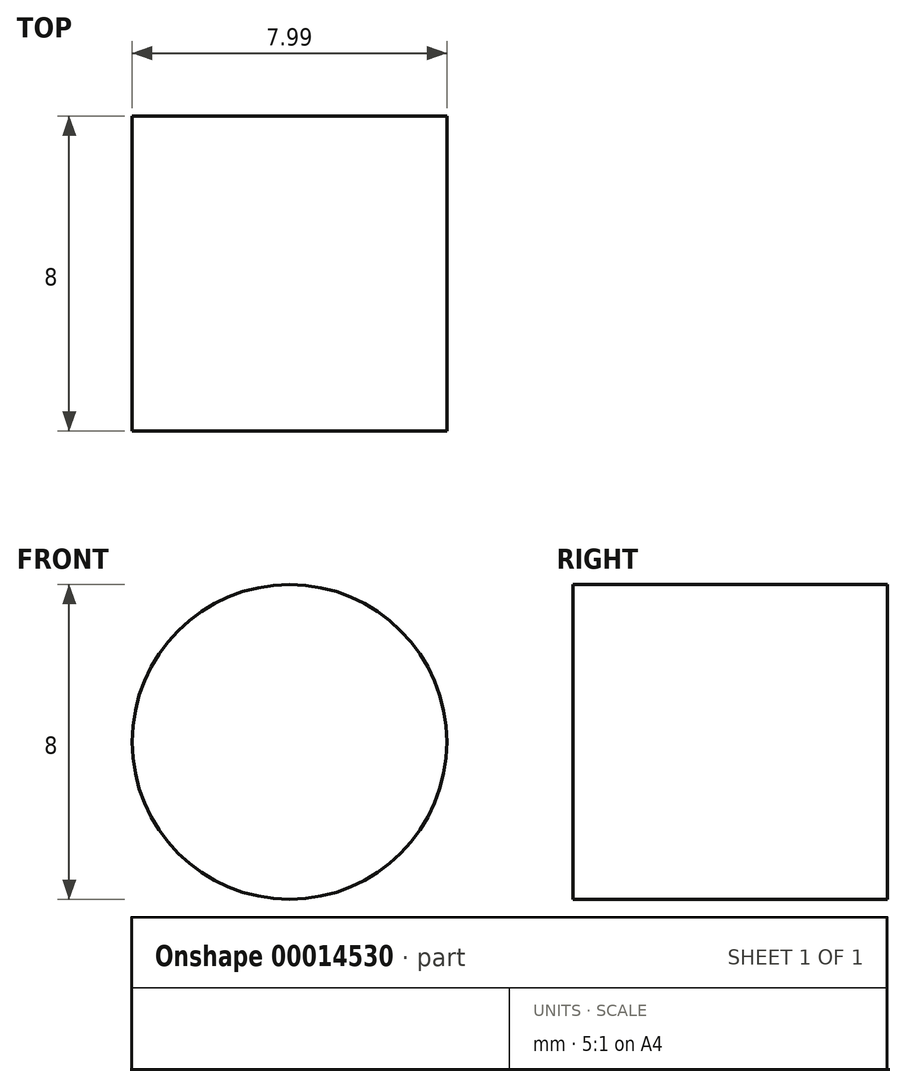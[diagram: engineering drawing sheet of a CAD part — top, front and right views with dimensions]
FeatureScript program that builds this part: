
annotation { "Feature Type Name" : "Feature", "Feature Type Description" : "" }
export const myFeature = defineFeature(function(context is Context, id is Id, definition is map)
    precondition{}
    {
        {
            var Q0;
            Q0=qCreatedBy(makeId("Front.planeOp"),FACE);
            var sketch = newSketch(context, id + "F0", { "sketchPlane" : qUnion([Q0])});
            skCircle(sketch, "E0", {"center": v(-38.94, 44.64) * mm, "radius": 4 * mm});
            skSolve(sketch);
        }
        {
            var Q0;
            Q0 = qSketchRegion(id + "F0", true);
            extrude(context, id + "F1", {"entities" : qUnion([Q0]), "depth" : 8 * mm});
        }
    });
